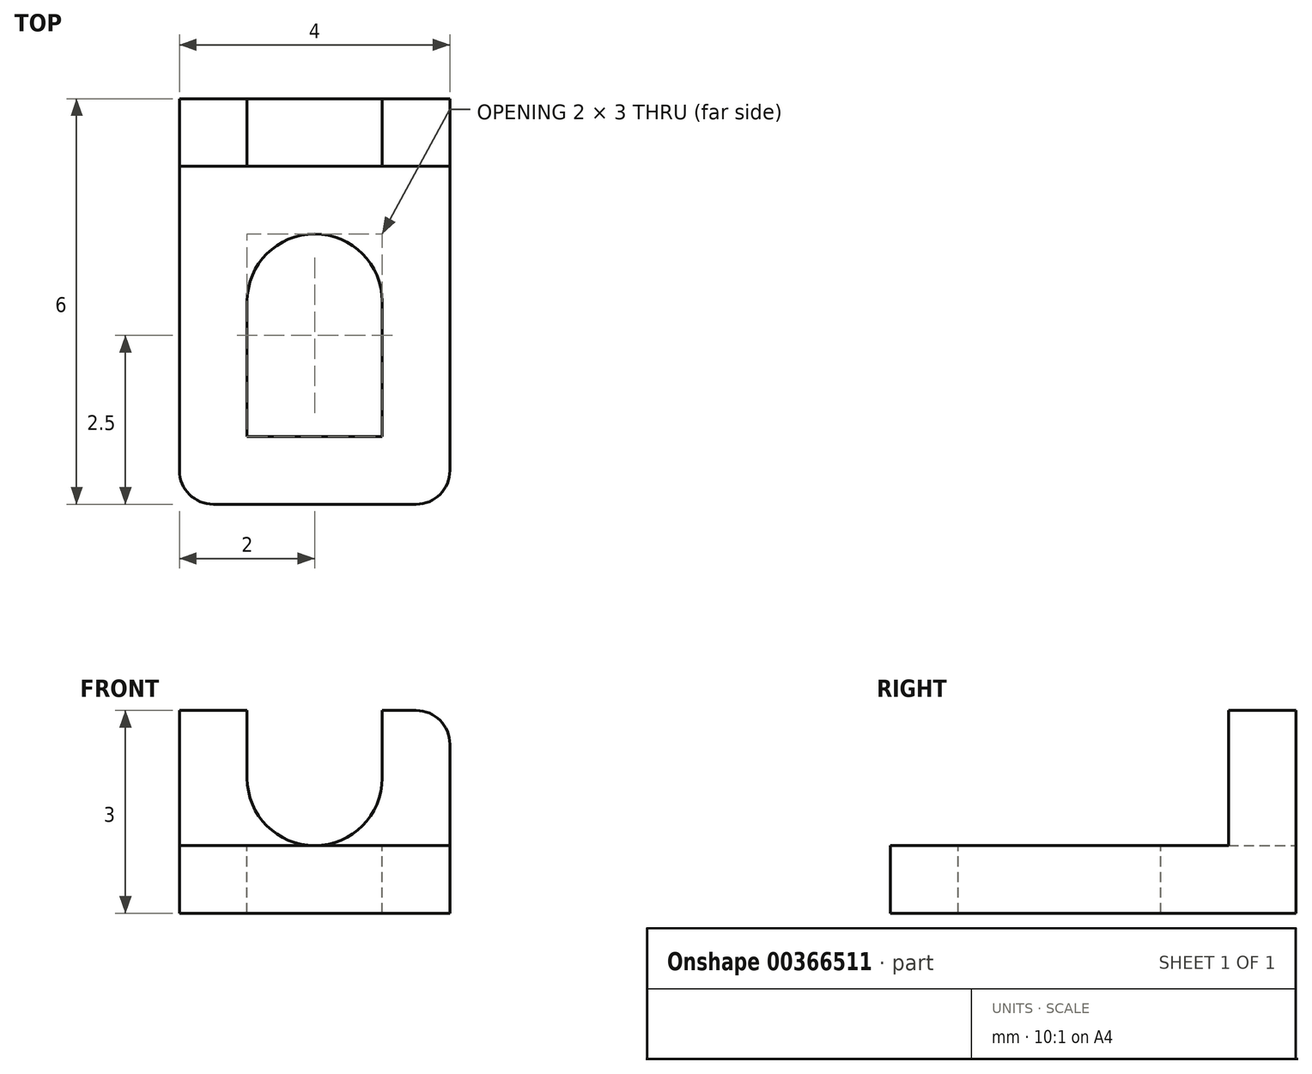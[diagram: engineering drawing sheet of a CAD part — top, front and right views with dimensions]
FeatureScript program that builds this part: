
annotation { "Feature Type Name" : "Feature", "Feature Type Description" : "" }
export const myFeature = defineFeature(function(context is Context, id is Id, definition is map)
    precondition{}
    {
        {
            var Q0;
            Q0=qCreatedBy(makeId("Front.planeOp"),FACE);
            var sketch = newSketch(context, id + "F0", { "sketchPlane" : qUnion([Q0])});
            skLineSegment(sketch, "E0", {"start": v(0, 0) * mm, "end": v(4, 0) * mm});
            skLineSegment(sketch, "E1", {"start": v(4, 0) * mm, "end": v(4, 3) * mm});
            skLineSegment(sketch, "E2", {"start": v(4, 3) * mm, "end": v(0, 3) * mm});
            skLineSegment(sketch, "E3", {"start": v(0, 3) * mm, "end": v(0, 0) * mm});
            skSolve(sketch);
        }
        {
            var Q0;
            Q0=qSketchRegion(id+"F0",true);
            extrude(context, id + "F1", {"entities" : qUnion([Q0]), "depth" : 6 * mm});
        }
        {
            var Q0;
            Q0=makeQuery(id+"F1.opExtrude","CAP_EDGE",EDGE,{"disambiguationData":[OSD([sQuery(id+"F0.wireOp",EDGE,"E1")])],"isStart":false});
            fillet(context, id + "F2", {"entities" : qUnion([Q0]), "radius" : 0.5 * mm, "tangentPropagation" : true, "allowEdgeOverflow" : false});
        }
        {
            var Q0;
            Q0=makeQuery(id+"F1.opExtrude","CAP_EDGE",EDGE,{"disambiguationData":[OSD([sQuery(id+"F0.wireOp",EDGE,"E3")])],"isStart":false});
            fillet(context, id + "F3", {"entities" : qUnion([Q0]), "radius" : 0.5 * mm, "tangentPropagation" : true, "allowEdgeOverflow" : false});
        }
        {
            var Q0;
            Q0=makeQuery(id+"F1.opExtrude","CAP_FACE",FACE,{"disambiguationData":[OSD([sQuery(id+"F0.wireOp",EDGE,"E0"),sQuery(id+"F0.wireOp",EDGE,"E1"),sQuery(id+"F0.wireOp",EDGE,"E2"),sQuery(id+"F0.wireOp",EDGE,"E3")])],"isStart":true});
            var sketch = newSketch(context, id + "F4", { "sketchPlane" : qUnion([Q0])});
            skLineSegment(sketch, "E4", {"start": v(0, 3) * mm, "end": v(-1, 3) * mm});
            skLineSegment(sketch, "E5", {"start": v(-1, 3) * mm, "end": v(-1, 2) * mm});
            skLineSegment(sketch, "E6", {"start": v(-1, 2) * mm, "end": v(-2, 2) * mm});
            skCircle(sketch, "E7", {"center": v(-2, 2) * mm, "radius": 1 * mm});
            skLineSegment(sketch, "E8", {"start": v(-2, 2) * mm, "end": v(-3, 2) * mm});
            skLineSegment(sketch, "E9", {"start": v(-3, 2) * mm, "end": v(-3, 3) * mm});
            skSolve(sketch);
        }
        {
            var Q0;
            Q0=qSketchRegion(id+"F4",true);
            var Q1;
            {var subQ0=sQuery(id+"F4.wireOp",EDGE,"E9");Q1=makeQuery(id+"F4.imprint","IMPRINT",FACE,{"disambiguationData":[TD([[makeQuery(id+"F4.imprint","IMPRINT",EDGE,{"derivedFrom":subQ0}),-1.0]])]});}
            var Q2;
            {var subQ0=sQuery(id+"F4.wireOp",EDGE,"E5");Q2=makeQuery(id+"F4.imprint","IMPRINT",FACE,{"disambiguationData":[TD([[makeQuery(id+"F4.imprint","IMPRINT",EDGE,{"derivedFrom":subQ0}),-1.0]])]});}
            extrude(context, id + "F5", {"entities" : qUnion([Q0, Q1, Q2]), "operationType" : NewBodyOperationType.REMOVE, "oppositeDirection" : true, "depth" : 25 * mm});
        }
        {
            var Q0;
            {var subQ0=sQuery(id+"F0.wireOp",EDGE,"E1");var subQ2=sQuery(id+"F0.wireOp",EDGE,"E2");Q0=makeQuery(id+"F5.boolean.opBoolean","SPLIT",FACE,{"disambiguationData":[TD([makeQuery(id+"F1.opExtrude","SWEPT_FACE",FACE,{"disambiguationData":[OSD([subQ0])]})])],"derivedFrom":makeQuery(id+"F1.opExtrude","SWEPT_FACE",FACE,{"disambiguationData":[OSD([subQ2])]})});}
            var sketch = newSketch(context, id + "F6", { "sketchPlane" : qUnion([Q0])});
            skLineSegment(sketch, "E10", {"start": v(4, 0) * mm, "end": v(4, -1) * mm});
            skLineSegment(sketch, "E11", {"start": v(4, -1) * mm, "end": v(0, -1) * mm});
            skLineSegment(sketch, "E12", {"start": v(4, -1) * mm, "end": v(4, -6.81) * mm});
            skLineSegment(sketch, "E13", {"start": v(4, -6.81) * mm, "end": v(0, -6.81) * mm});
            skLineSegment(sketch, "E14", {"start": v(0, -6.81) * mm, "end": v(0, -1) * mm});
            skSolve(sketch);
        }
        {
            var Q0;
            Q0=qSketchRegion(id+"F6",true);
            extrude(context, id + "F7", {"entities" : qUnion([Q0]), "operationType" : NewBodyOperationType.REMOVE, "oppositeDirection" : true, "depth" : 2 * mm});
        }
        {
            var Q0;
            Q0=makeQuery(id+"F1.opExtrude","SWEPT_EDGE",EDGE,{"disambiguationData":[OSD([sQuery(id+"F0.wireOp",EDGE,"E1"),sQuery(id+"F0.wireOp",EDGE,"E2")])]});
            fillet(context, id + "F8", {"entities" : qUnion([Q0]), "radius" : 0.5 * mm, "tangentPropagation" : true, "allowEdgeOverflow" : false});
        }
        {
            var Q0;
            Q0=makeQuery(id+"F7.boolean.opBoolean","COPY",FACE,{"derivedFrom":makeQuery(id+"F7.opExtrude","CAP_FACE",FACE,{"disambiguationData":[OSD([sQuery(id+"F6.wireOp",EDGE,"E11"),sQuery(id+"F6.wireOp",EDGE,"E12"),sQuery(id+"F6.wireOp",EDGE,"E13"),sQuery(id+"F6.wireOp",EDGE,"E14")])],"isStart":false})});
            var sketch = newSketch(context, id + "F9", { "sketchPlane" : qUnion([Q0])});
            skCircle(sketch, "E15", {"center": v(2, -3) * mm, "radius": 1 * mm});
            skLineSegment(sketch, "E16", {"start": v(3, -3) * mm, "end": v(3, -6) * mm});
            skLineSegment(sketch, "E17", {"start": v(1, -3) * mm, "end": v(1, -6) * mm});
            skLineSegment(sketch, "E18", {"start": v(1, -6) * mm, "end": v(1, -5) * mm});
            skLineSegment(sketch, "E19", {"start": v(1, -5) * mm, "end": v(3, -5) * mm});
            skSolve(sketch);
        }
        {
            var Q0;
            Q0=qSketchRegion(id+"F9",true);
            extrude(context, id + "F10", {"entities" : qUnion([Q0]), "operationType" : NewBodyOperationType.REMOVE, "oppositeDirection" : true, "depth" : 25 * mm});
        }
    });
